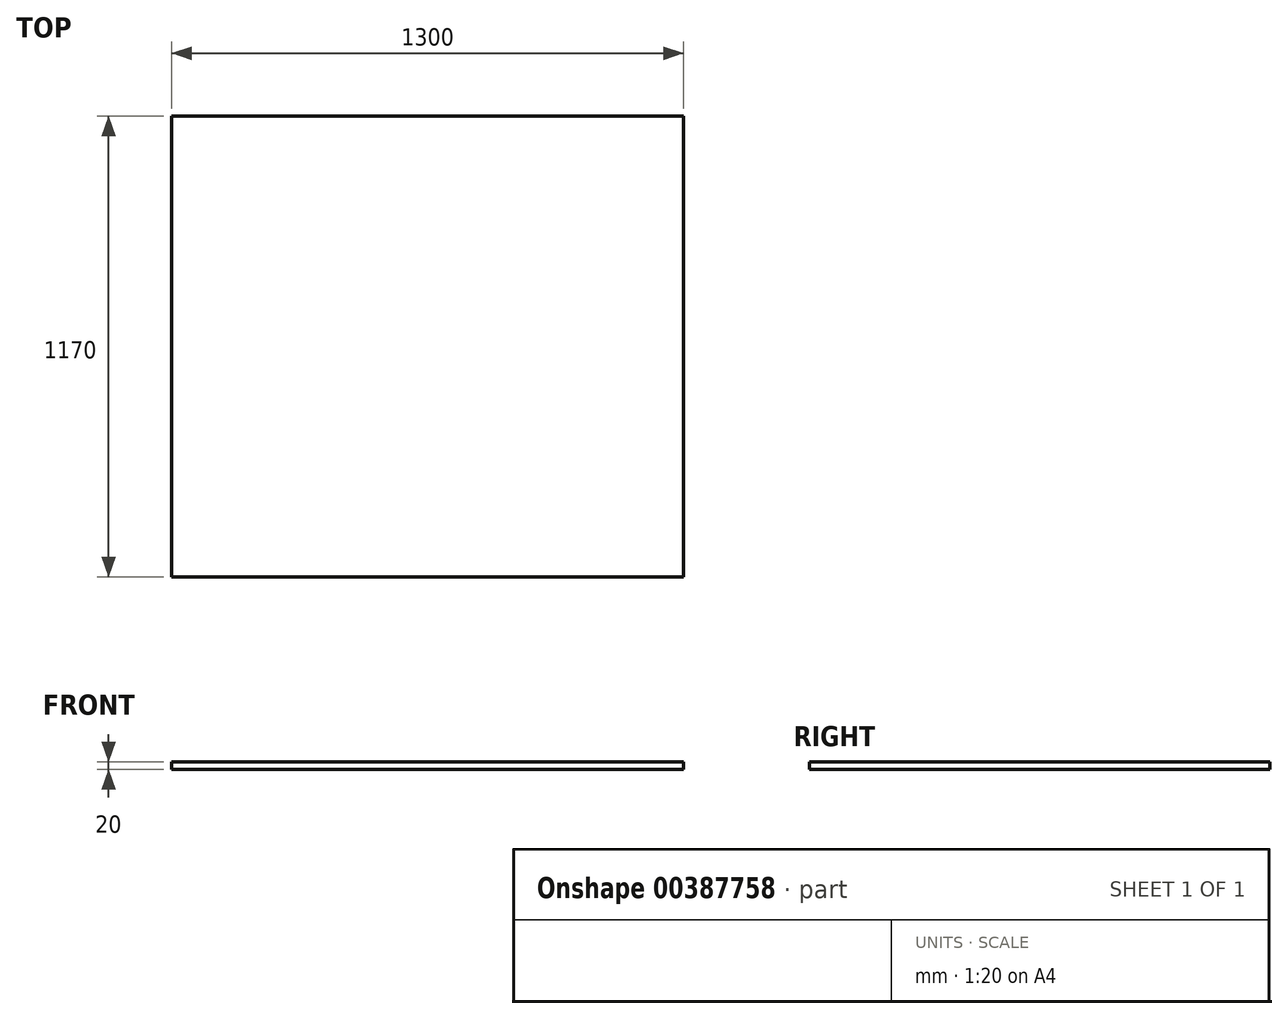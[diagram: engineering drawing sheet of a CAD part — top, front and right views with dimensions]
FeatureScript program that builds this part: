
annotation { "Feature Type Name" : "Feature", "Feature Type Description" : "" }
export const myFeature = defineFeature(function(context is Context, id is Id, definition is map)
    precondition{}
    {
        {
            var Q0;
            Q0=qCreatedBy(makeId("Top.planeOp"),FACE);
            var sketch = newSketch(context, id + "F0", { "sketchPlane" : qUnion([Q0])});
            skLineSegment(sketch, "E0.bottom", {"start": v(0, 0) * mm, "end": v(1300, 0) * mm});
            skLineSegment(sketch, "E0.top", {"start": v(0, 1170) * mm, "end": v(1300, 1170) * mm});
            skLineSegment(sketch, "E0.left", {"start": v(0, 0) * mm, "end": v(0, 1170) * mm});
            skLineSegment(sketch, "E0.right", {"start": v(1300, 0) * mm, "end": v(1300, 1170) * mm});
            skSolve(sketch);
        }
        {
            var Q0;
            Q0=makeQuery(id+"F0.imprint","IMPRINT",FACE,{"disambiguationData":[TD([[makeQuery(id+"F0.imprint","IMPRINT",EDGE,{"derivedFrom":sQuery(id+"F0.wireOp",EDGE,"E0.bottom")}),1.0]])]});
            extrude(context, id + "F1", {"entities" : qUnion([Q0]), "depth" : 20 * mm});
        }
    });
